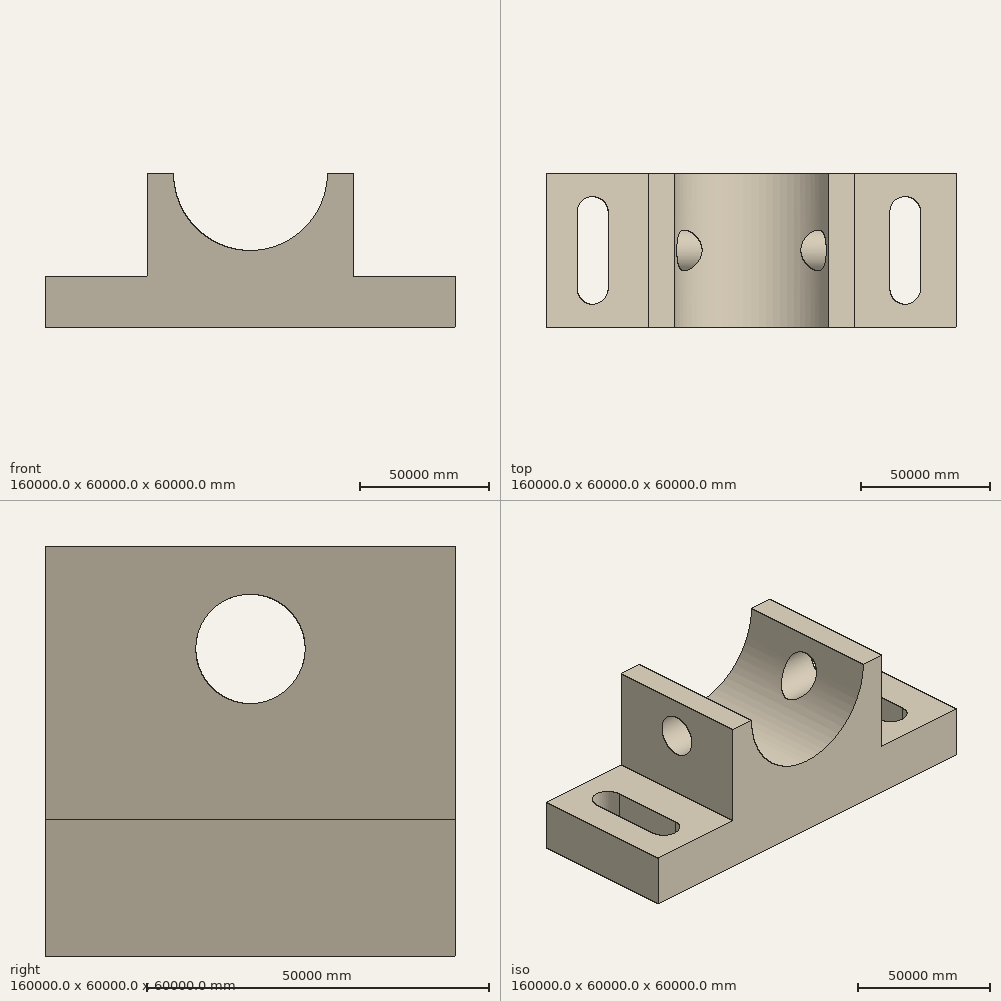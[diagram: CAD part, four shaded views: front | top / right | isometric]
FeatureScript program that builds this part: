
annotation { "Feature Type Name" : "Feature", "Feature Type Description" : "" }
export const myFeature = defineFeature(function(context is Context, id is Id, definition is map)
    precondition{}
    {
        {
            var Q0;
            Q0=qCreatedBy(makeId("Front.planeOp"),FACE);
            var sketch = newSketch(context, id + "F0", { "sketchPlane" : qUnion([Q0])});
            skLineSegment(sketch, "E0.bottom", {"start": v(-80000, -10000) * mm, "end": v(80000, -10000) * mm});
            skLineSegment(sketch, "E0.top", {"start": v(-80000, 10000) * mm, "end": v(-40000, 10000) * mm});
            skLineSegment(sketch, "E0.left", {"start": v(-80000, -10000) * mm, "end": v(-80000, 10000) * mm});
            skLineSegment(sketch, "E0.right", {"start": v(80000, -10000) * mm, "end": v(80000, 10000) * mm});
            skPoint(sketch, "E0.middle", {"position": v(0, 0) * mm});
            skLineSegment(sketch, "E1", {"start": v(-40000, 10000) * mm, "end": v(-40000, 50000) * mm});
            skLineSegment(sketch, "E2", {"start": v(-40000, 50000) * mm, "end": v(-30000, 50000) * mm});
            skLineSegment(sketch, "E3", {"start": v(40000, 50000) * mm, "end": v(40000, 10000) * mm});
            skLineSegment(sketch, "E4", {"start": v(40000, 50000) * mm, "end": v(30000, 50000) * mm});
            skArc(sketch, "E5", {"start": v(-30000, 50000) * mm, "mid": v(0, 20000) * mm, "end": v(30000, 50000) * mm});
            skPoint(sketch, "E6.orphan", {"position": v(30837.23, 50000) * mm});
            skLineSegment(sketch, "E7.trimOffspring", {"start": v(40000, 10000) * mm, "end": v(80000, 10000) * mm});
            skSolve(sketch);
        }
        {
            var Q0;
            Q0 = qSketchRegion(id + "F0", true);
            extrude(context, id + "F1", {"entities" : qUnion([Q0]), "depth" : 60000 * mm, "offsetDistance" : 25 * mm});
        }
        {
            var Q0;
            Q0=makeQuery(id+"F1.opExtrude","SWEPT_FACE",FACE,{"disambiguationData":[OSD([sQuery(id+"F0.wireOp",EDGE,"E1")])]});
            var sketch = newSketch(context, id + "F2", { "sketchPlane" : qUnion([Q0])});
            skCircle(sketch, "E8", {"center": v(30000, 35000) * mm, "radius": 8000 * mm});
            skPoint(sketch, "E8.centerSnap0", {"position": v(30000, 50000) * mm});
            skSolve(sketch);
        }
        {
            var Q0;
            Q0 = qSketchRegion(id + "F2", true);
            extrude(context, id + "F3", {"entities" : qUnion([Q0]), "operationType" : NewBodyOperationType.REMOVE, "endBound" : BoundingType.THROUGH_ALL, "oppositeDirection" : true, "depth" : 25 * mm, "offsetDistance" : 25 * mm});
        }
        {
            var Q0;
            Q0=makeQuery(id+"F1.opExtrude","SWEPT_FACE",FACE,{"disambiguationData":[OSD([sQuery(id+"F0.wireOp",EDGE,"E7.trimOffspring")])]});
            var sketch = newSketch(context, id + "F4", { "sketchPlane" : qUnion([Q0])});
            skLineSegment(sketch, "E9.left", {"start": v(54000, -45000) * mm, "end": v(54000, -15000) * mm});
            skLineSegment(sketch, "E9.right", {"start": v(66000, -45000) * mm, "end": v(66000, -15000) * mm});
            skPoint(sketch, "E9.middle", {"position": v(60000, -30000) * mm});
            skPoint(sketch, "E9.middle.positionSnap0", {"position": v(80000, -30000) * mm});
            skPoint(sketch, "E9.middle.positionSnap1", {"position": v(60000, 0) * mm});
            skPoint(sketch, "E9.centerSnap0", {"position": v(80000, -30000) * mm});
            skPoint(sketch, "E9.centerSnap1", {"position": v(60000, 0) * mm});
            skArc(sketch, "E10", {"start": v(66000, -15000) * mm, "mid": v(60000, -9000) * mm, "end": v(54000, -15000) * mm});
            skArc(sketch, "E11", {"start": v(54000, -45000) * mm, "mid": v(60000, -51000) * mm, "end": v(66000, -45000) * mm});
            skLineSegment(sketch, "E12.left", {"start": v(-67931.56, -45000) * mm, "end": v(-67931.56, -15000) * mm});
            skLineSegment(sketch, "E12.right", {"start": v(-55931.56, -45000) * mm, "end": v(-55931.56, -15000) * mm});
            skPoint(sketch, "E12.middle", {"position": v(-61931.56, -30000) * mm});
            skPoint(sketch, "E12.middle.positionSnap0", {"position": v(54000, -30000) * mm});
            skPoint(sketch, "E12.centerSnap0", {"position": v(54000, -30000) * mm});
            skArc(sketch, "E13", {"start": v(-55931.56, -15000) * mm, "mid": v(-61931.56, -9000) * mm, "end": v(-67931.56, -15000) * mm});
            skArc(sketch, "E14", {"start": v(-67931.56, -45000) * mm, "mid": v(-61931.56, -51000) * mm, "end": v(-55931.56, -45000) * mm});
            skSolve(sketch);
        }
        {
            var Q0;
            Q0 = qSketchRegion(id + "F4", true);
            extrude(context, id + "F5", {"entities" : qUnion([Q0]), "operationType" : NewBodyOperationType.REMOVE, "endBound" : BoundingType.THROUGH_ALL, "oppositeDirection" : true, "depth" : 25 * mm, "offsetDistance" : 25 * mm});
        }
    });
